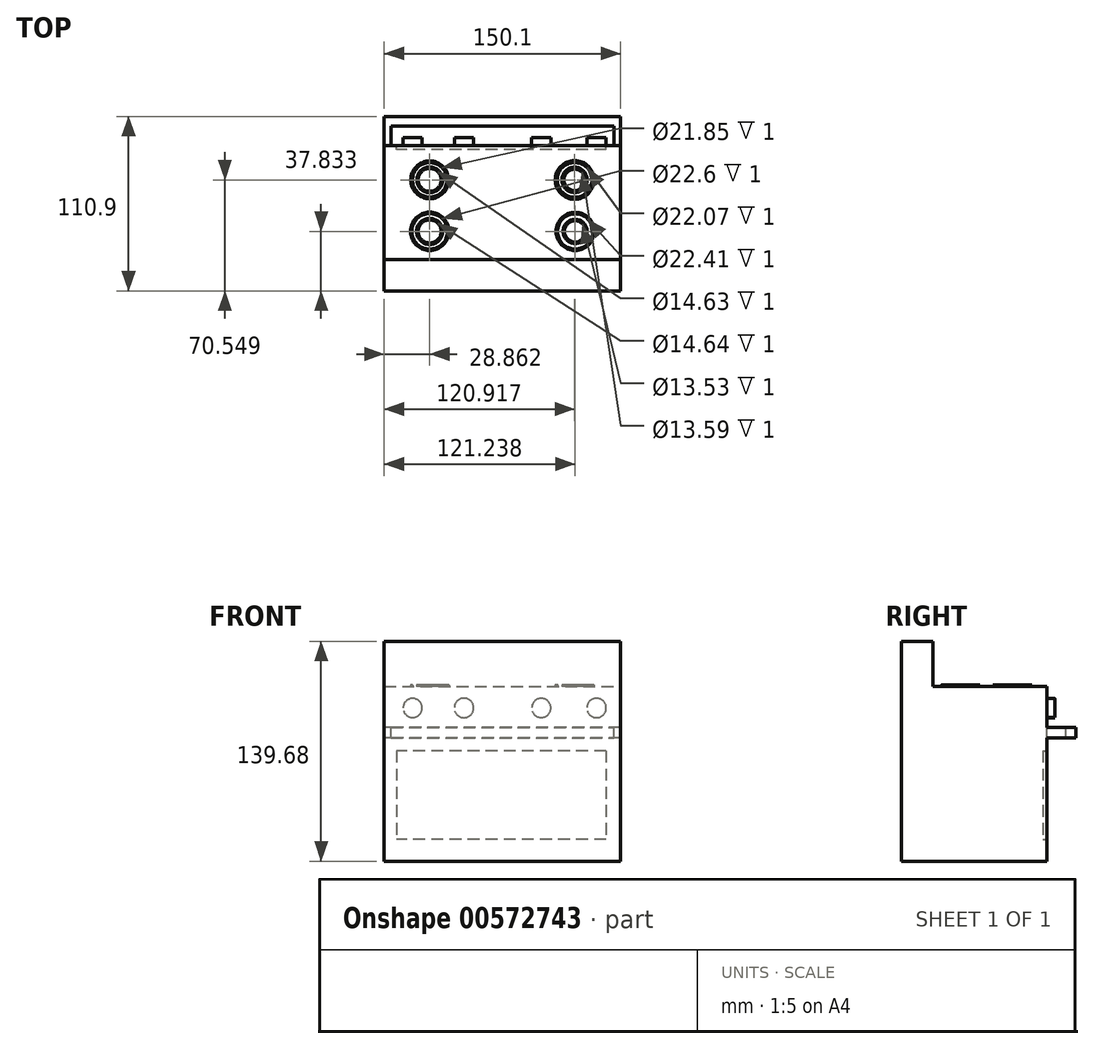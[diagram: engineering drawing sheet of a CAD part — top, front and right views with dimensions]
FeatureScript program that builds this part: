
annotation { "Feature Type Name" : "Feature", "Feature Type Description" : "" }
export const myFeature = defineFeature(function(context is Context, id is Id, definition is map)
    precondition{}
    {
        {
            var Q0;
            Q0=qCreatedBy(makeId("Front.planeOp"),FACE);
            var sketch = newSketch(context, id + "F0", { "sketchPlane" : qUnion([Q0])});
            skLineSegment(sketch, "E0.bottom", {"start": v(-75.05, 55.5) * mm, "end": v(75.05, 55.5) * mm});
            skLineSegment(sketch, "E0.top", {"start": v(-75.05, -55.5) * mm, "end": v(75.05, -55.5) * mm});
            skLineSegment(sketch, "E0.left", {"start": v(-75.05, 55.5) * mm, "end": v(-75.05, -55.5) * mm});
            skLineSegment(sketch, "E0.right", {"start": v(75.05, 55.5) * mm, "end": v(75.05, -55.5) * mm});
            skPoint(sketch, "E0.middle", {"position": v(0, 0) * mm});
            skSolve(sketch);
        }
        {
            var Q0;
            Q0=makeQuery(id+"F0.imprint","IMPRINT",FACE,{"disambiguationData":[TD([[makeQuery(id+"F0.imprint","IMPRINT",EDGE,{"derivedFrom":sQuery(id+"F0.wireOp",EDGE,"E0.bottom")}),-1.0]])]});
            extrude(context, id + "F1", {"entities" : qUnion([Q0]), "depth" : 92.4 * mm, "offsetDistance" : 25 * mm});
        }
        {
            var Q0;
            Q0=makeQuery(id+"F1.opExtrude","SWEPT_FACE",FACE,{"disambiguationData":[OSD([sQuery(id+"F0.wireOp",EDGE,"E0.bottom")])]});
            var sketch = newSketch(context, id + "F2", { "sketchPlane" : qUnion([Q0])});
            skLineSegment(sketch, "E1.bottom", {"start": v(-75.05, -92.4) * mm, "end": v(75.58, -92.4) * mm});
            skLineSegment(sketch, "E1.top", {"start": v(-75.05, -72.4) * mm, "end": v(75.58, -72.4) * mm});
            skLineSegment(sketch, "E1.left", {"start": v(-75.05, -92.4) * mm, "end": v(-75.05, -72.4) * mm});
            skLineSegment(sketch, "E1.right", {"start": v(75.58, -92.4) * mm, "end": v(75.58, -72.4) * mm});
            skSolve(sketch);
        }
        {
            var Q0;
            {var subQ0=sQuery(id+"F2.wireOp",EDGE,"E1.left");Q0=makeQuery(id+"F2.imprint","IMPRINT",FACE,{"disambiguationData":[TD([[makeQuery(id+"F2.imprint","IMPRINT",EDGE,{"derivedFrom":subQ0}),-1.0]])]});}
            extrude(context, id + "F3", {"entities" : qUnion([Q0]), "operationType" : NewBodyOperationType.ADD, "depth" : 28.7 * mm, "offsetDistance" : 25 * mm});
        }
        {
            var Q0;
            Q0=makeQuery(id+"F1.opExtrude","CAP_FACE",FACE,{"disambiguationData":[OSD([sQuery(id+"F0.wireOp",EDGE,"E0.bottom"),sQuery(id+"F0.wireOp",EDGE,"E0.top"),sQuery(id+"F0.wireOp",EDGE,"E0.left"),sQuery(id+"F0.wireOp",EDGE,"E0.right")])],"isStart":true});
            var sketch = newSketch(context, id + "F4", { "sketchPlane" : qUnion([Q0])});
            skLineSegment(sketch, "E2.bottom", {"start": v(-75.05, 29.56) * mm, "end": v(75.05, 29.56) * mm});
            skLineSegment(sketch, "E2.top", {"start": v(-75.05, 22.83) * mm, "end": v(75.05, 22.83) * mm});
            skLineSegment(sketch, "E2.left", {"start": v(-75.05, 29.56) * mm, "end": v(-75.05, 22.83) * mm});
            skLineSegment(sketch, "E2.right", {"start": v(75.05, 29.56) * mm, "end": v(75.05, 22.83) * mm});
            skPoint(sketch, "E2.middle", {"position": v(0, 26.2) * mm});
            skSolve(sketch);
        }
        {
            var Q0;
            Q0=makeQuery(id+"F4.imprint","IMPRINT",FACE,{"disambiguationData":[TD([[makeQuery(id+"F4.imprint","IMPRINT",EDGE,{"derivedFrom":sQuery(id+"F4.wireOp",EDGE,"E2.bottom")}),-1.0]])]});
            extrude(context, id + "F5", {"entities" : qUnion([Q0]), "operationType" : NewBodyOperationType.ADD, "depth" : 18.5 * mm, "offsetDistance" : 25 * mm});
        }
        {
            var Q0;
            Q0=makeQuery(id+"F5.opExtrude","SWEPT_FACE",FACE,{"disambiguationData":[OSD([sQuery(id+"F4.wireOp",EDGE,"E2.bottom")])]});
            var sketch = newSketch(context, id + "F6", { "sketchPlane" : qUnion([Q0])});
            skLineSegment(sketch, "E3.bottom", {"start": v(-70.78, 12.24) * mm, "end": v(70.78, 12.24) * mm});
            skLineSegment(sketch, "E3.top", {"start": v(-70.78, 0) * mm, "end": v(70.78, 0) * mm});
            skLineSegment(sketch, "E3.left", {"start": v(-70.78, 12.24) * mm, "end": v(-70.78, 0) * mm});
            skLineSegment(sketch, "E3.right", {"start": v(70.78, 12.24) * mm, "end": v(70.78, 0) * mm});
            skSolve(sketch);
        }
        {
            var Q0;
            Q0=makeQuery(id+"F6.imprint","IMPRINT",FACE,{"disambiguationData":[TD([[makeQuery(id+"F6.imprint","IMPRINT",EDGE,{"derivedFrom":sQuery(id+"F6.wireOp",EDGE,"E3.bottom")}),-1.0]])]});
            extrude(context, id + "F7", {"entities" : qUnion([Q0]), "operationType" : NewBodyOperationType.REMOVE, "oppositeDirection" : true, "depth" : 9.7 * mm, "offsetDistance" : 25 * mm});
        }
        {
            var Q0;
            {var subQ1=sQuery(id+"F0.wireOp",EDGE,"E0.right");var subQ3=sQuery(id+"F0.wireOp",EDGE,"E0.left");var subQ5=sQuery(id+"F0.wireOp",EDGE,"E0.top");var subQ6=sQuery(id+"F0.wireOp",EDGE,"E0.bottom");var subQ10=makeQuery(id+"F1.opExtrude","CAP_FACE",FACE,{"disambiguationData":[OSD([subQ6,subQ5,subQ3,subQ1])],"isStart":true});Q0=makeQuery(id+"F7.boolean.opBoolean","MERGE",FACE,{"derivedFrom":[makeQuery(id+"F5.boolean.opBoolean","SPLIT",FACE,{"disambiguationData":[TD([makeQuery(id+"F1.opExtrude","SWEPT_FACE",FACE,{"disambiguationData":[OSD([subQ6])]})])],"derivedFrom":subQ10}),makeQuery(id+"F5.boolean.opBoolean","SPLIT",FACE,{"disambiguationData":[TD([makeQuery(id+"F1.opExtrude","SWEPT_FACE",FACE,{"disambiguationData":[OSD([subQ5])]})])],"derivedFrom":subQ10}),makeQuery(id+"F7.opExtrude","SWEPT_FACE",FACE,{"disambiguationData":[OSD([sQuery(id+"F6.wireOp",EDGE,"E3.top")])]})]});}
            var sketch = newSketch(context, id + "F8", { "sketchPlane" : qUnion([Q0])});
            skLineSegment(sketch, "E4.bottom", {"start": v(-65.89, 14.66) * mm, "end": v(67.1, 14.66) * mm});
            skLineSegment(sketch, "E4.top", {"start": v(-65.89, -41.77) * mm, "end": v(67.1, -41.77) * mm});
            skLineSegment(sketch, "E4.left", {"start": v(-65.89, 14.66) * mm, "end": v(-65.89, -41.77) * mm});
            skLineSegment(sketch, "E4.right", {"start": v(67.1, 14.66) * mm, "end": v(67.1, -41.77) * mm});
            skSolve(sketch);
        }
        {
            var Q0;
            Q0=makeQuery(id+"F8.imprint","IMPRINT",FACE,{"disambiguationData":[TD([[makeQuery(id+"F8.imprint","IMPRINT",EDGE,{"derivedFrom":sQuery(id+"F8.wireOp",EDGE,"E4.bottom")}),-1.0]])]});
            extrude(context, id + "F9", {"entities" : qUnion([Q0]), "operationType" : NewBodyOperationType.REMOVE, "oppositeDirection" : true, "depth" : 2.5 * mm, "offsetDistance" : 25 * mm});
        }
        {
            var Q0;
            {var subQ1=sQuery(id+"F0.wireOp",EDGE,"E0.right");var subQ3=sQuery(id+"F0.wireOp",EDGE,"E0.left");var subQ5=sQuery(id+"F0.wireOp",EDGE,"E0.top");var subQ6=sQuery(id+"F0.wireOp",EDGE,"E0.bottom");var subQ10=makeQuery(id+"F1.opExtrude","CAP_FACE",FACE,{"disambiguationData":[OSD([subQ6,subQ5,subQ3,subQ1])],"isStart":true});Q0=makeQuery(id+"F7.boolean.opBoolean","MERGE",FACE,{"derivedFrom":[makeQuery(id+"F5.boolean.opBoolean","SPLIT",FACE,{"disambiguationData":[TD([makeQuery(id+"F1.opExtrude","SWEPT_FACE",FACE,{"disambiguationData":[OSD([subQ6])]})])],"derivedFrom":subQ10}),makeQuery(id+"F5.boolean.opBoolean","SPLIT",FACE,{"disambiguationData":[TD([makeQuery(id+"F1.opExtrude","SWEPT_FACE",FACE,{"disambiguationData":[OSD([subQ5])]})])],"derivedFrom":subQ10}),makeQuery(id+"F7.opExtrude","SWEPT_FACE",FACE,{"disambiguationData":[OSD([sQuery(id+"F6.wireOp",EDGE,"E3.top")])]})]});}
            var sketch = newSketch(context, id + "F10", { "sketchPlane" : qUnion([Q0])});
            skCircle(sketch, "E5", {"center": v(-24.7, 41.81) * mm, "radius": 6.08 * mm});
            skCircle(sketch, "E6", {"center": v(24.4, 41.81) * mm, "radius": 6.17 * mm});
            skCircle(sketch, "E7", {"center": v(-59.79, 41.81) * mm, "radius": 6.13 * mm});
            skCircle(sketch, "E8", {"center": v(57.04, 41.81) * mm, "radius": 6 * mm});
            skSolve(sketch);
        }
        {
            var Q0;
            Q0=makeQuery(id+"F10.imprint","IMPRINT",FACE,{"disambiguationData":[TD([[makeQuery(id+"F10.imprint","IMPRINT",EDGE,{"derivedFrom":sQuery(id+"F10.wireOp",EDGE,"E5")}),1.0]])]});
            var Q1;
            Q1=makeQuery(id+"F10.imprint","IMPRINT",FACE,{"disambiguationData":[TD([[makeQuery(id+"F10.imprint","IMPRINT",EDGE,{"derivedFrom":sQuery(id+"F10.wireOp",EDGE,"E7")}),1.0]])]});
            var Q2;
            Q2=makeQuery(id+"F10.imprint","IMPRINT",FACE,{"disambiguationData":[TD([[makeQuery(id+"F10.imprint","IMPRINT",EDGE,{"derivedFrom":sQuery(id+"F10.wireOp",EDGE,"E6")}),1.0]])]});
            var Q3;
            Q3=makeQuery(id+"F10.imprint","IMPRINT",FACE,{"disambiguationData":[TD([[makeQuery(id+"F10.imprint","IMPRINT",EDGE,{"derivedFrom":sQuery(id+"F10.wireOp",EDGE,"E8")}),1.0]])]});
            extrude(context, id + "F11", {"entities" : qUnion([Q0, Q1, Q2, Q3]), "operationType" : NewBodyOperationType.ADD, "depth" : 5 * mm, "offsetDistance" : 25 * mm});
        }
        {
            var Q0;
            Q0=makeQuery(id+"F1.opExtrude","SWEPT_FACE",FACE,{"disambiguationData":[OSD([sQuery(id+"F0.wireOp",EDGE,"E0.bottom")])]});
            var sketch = newSketch(context, id + "F12", { "sketchPlane" : qUnion([Q0])});
            skCircle(sketch, "E9", {"center": v(-46.19, -21.85) * mm, "radius": 12.02 * mm});
            skCircle(sketch, "E10", {"center": v(-46.19, -54.57) * mm, "radius": 12.2 * mm});
            skCircle(sketch, "E11", {"center": v(45.87, -21.85) * mm, "radius": 12.32 * mm});
            skCircle(sketch, "E12", {"center": v(46.19, -54.57) * mm, "radius": 12.1 * mm});
            skCircle(sketch, "E13", {"center": v(-46.19, -21.85) * mm, "radius": 10.92 * mm});
            skCircle(sketch, "E14", {"center": v(-46.19, -21.85) * mm, "radius": 8.18 * mm});
            skCircle(sketch, "E15", {"center": v(-46.19, -21.85) * mm, "radius": 7.31 * mm});
            skCircle(sketch, "E16", {"center": v(-46.19, -54.57) * mm, "radius": 11.3 * mm});
            skCircle(sketch, "E17", {"center": v(-46.19, -54.57) * mm, "radius": 8.32 * mm});
            skCircle(sketch, "E18", {"center": v(-46.19, -54.57) * mm, "radius": 7.32 * mm});
            skCircle(sketch, "E19", {"center": v(46.19, -54.57) * mm, "radius": 11.2 * mm});
            skCircle(sketch, "E20", {"center": v(46.19, -54.57) * mm, "radius": 7.65 * mm});
            skCircle(sketch, "E21", {"center": v(46.19, -54.57) * mm, "radius": 6.77 * mm});
            skCircle(sketch, "E22", {"center": v(45.87, -21.85) * mm, "radius": 11.04 * mm});
            skCircle(sketch, "E23", {"center": v(45.87, -21.85) * mm, "radius": 8.04 * mm});
            skCircle(sketch, "E24", {"center": v(45.87, -21.85) * mm, "radius": 6.8 * mm});
            skSolve(sketch);
        }
        {
            var Q0;
            Q0=makeQuery(id+"F12.imprint","IMPRINT",FACE,{"disambiguationData":[TD([[makeQuery(id+"F12.imprint","IMPRINT",EDGE,{"derivedFrom":sQuery(id+"F12.wireOp",EDGE,"E9")}),1.0]])]});
            var Q1;
            Q1=makeQuery(id+"F12.imprint","IMPRINT",FACE,{"disambiguationData":[TD([[makeQuery(id+"F12.imprint","IMPRINT",EDGE,{"derivedFrom":sQuery(id+"F12.wireOp",EDGE,"E14")}),1.0]])]});
            var Q2;
            Q2=makeQuery(id+"F12.imprint","IMPRINT",FACE,{"disambiguationData":[TD([[makeQuery(id+"F12.imprint","IMPRINT",EDGE,{"derivedFrom":sQuery(id+"F12.wireOp",EDGE,"E17")}),1.0]])]});
            var Q3;
            Q3=makeQuery(id+"F12.imprint","IMPRINT",FACE,{"disambiguationData":[TD([[makeQuery(id+"F12.imprint","IMPRINT",EDGE,{"derivedFrom":sQuery(id+"F12.wireOp",EDGE,"E10")}),1.0]])]});
            var Q4;
            Q4=makeQuery(id+"F12.imprint","IMPRINT",FACE,{"disambiguationData":[TD([[makeQuery(id+"F12.imprint","IMPRINT",EDGE,{"derivedFrom":sQuery(id+"F12.wireOp",EDGE,"E23")}),1.0]])]});
            var Q5;
            Q5=makeQuery(id+"F12.imprint","IMPRINT",FACE,{"disambiguationData":[TD([[makeQuery(id+"F12.imprint","IMPRINT",EDGE,{"derivedFrom":sQuery(id+"F12.wireOp",EDGE,"E11")}),1.0]])]});
            var Q6;
            Q6=makeQuery(id+"F12.imprint","IMPRINT",FACE,{"disambiguationData":[TD([[makeQuery(id+"F12.imprint","IMPRINT",EDGE,{"derivedFrom":sQuery(id+"F12.wireOp",EDGE,"E12")}),1.0]])]});
            var Q7;
            Q7=makeQuery(id+"F12.imprint","IMPRINT",FACE,{"disambiguationData":[TD([[makeQuery(id+"F12.imprint","IMPRINT",EDGE,{"derivedFrom":sQuery(id+"F12.wireOp",EDGE,"E20")}),1.0]])]});
            extrude(context, id + "F13", {"entities" : qUnion([Q0, Q1, Q2, Q3, Q4, Q5, Q6, Q7]), "operationType" : NewBodyOperationType.ADD, "depth" : 1 * mm, "offsetDistance" : 25 * mm});
        }
    });
